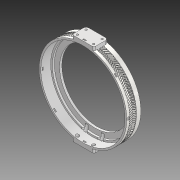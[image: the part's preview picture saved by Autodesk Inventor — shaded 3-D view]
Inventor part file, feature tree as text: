
AUTODESK INVENTOR PART (.ipt)
format: ipt  version: 2020 (Build 240168000, 168)  size: 2,971,648 bytes
history: native  units: in
note: dims shown in document units (in); Inventor stores cm internally (conversion verified against a paired STEP export)
features: other x5, extrude x5, sketch x5, plane x3, fillet x2, mirror x1
ambient origin geometry x8: Origin, YZ Plane, XZ Plane, XY Plane, X Axis, Y Axis, Z Axis, Center Point
bodies: Solid2 (feature_tree), Solid1 (feature_tree)
feature tree (21):
  other  "Blocks"
  extrude  "Extrusion1"  Depth=0.3543in
  extrude  "Extrusion3"  Depth=3.1496in
  plane  "Work Plane1"
  extrude  "Extrusion4"  Depth=0.4724in
  extrude  "Extrusion5"  Depth=1.1024in
  plane  "Work Plane2"
  extrude  "Extrusion6"  Depth=0.1181in TaperAngle=0.0deg
  fillet  "Fillet1"  [1 undecoded]
  mirror  "Mirror1"
  fillet  "Fillet2"  Radius=0.2362in
  sketch  "Sketch1"  dims[d0=0.0in d1=0.0in d5=0.3543in]
  sketch  "Sketch3"  dims[d6=0.1575in d7=0.0in d8=3.1496in]
  sketch  "Sketch4"  dims[d9=0.1575in d10=0.0in d11=0.4724in]
  other  "Block1"
  other  "Block2"
  sketch  "Sketch5"  dims[d12=0.5906in d13=1.1024in]
  sketch  "Sketch6"  dims[d14=0.1378in d15=0.6299in d16=0.0in d17=-0.1969in d18=0.2362in d19=0.3937in d20=0.0in d21=0.0787in d22=0.1181in]
  plane  "Work Plane3"
  other  "Block2:1"
  other  "Block1:2"
note: 1 required parameter value undecoded (feature->parameter linkage not recoverable at this tier; creation-order binding heuristic only, values carry confidence <= 0.55)
